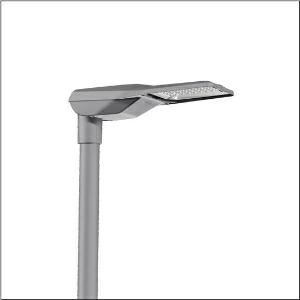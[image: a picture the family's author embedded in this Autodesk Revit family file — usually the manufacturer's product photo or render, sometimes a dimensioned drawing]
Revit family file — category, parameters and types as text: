
# Revit family: streetlight_sl_21_iq_mini___st0_5a_5xe2b41g08jb_20f7
name_source: partatom
category: Lighting Fixtures
units: mm (PartAtom-declared; Revit-internal decimal feet)

## family parameters
Cut with Voids When Loaded = No
Host = Face
Light Source = No
Part Type = Normal
Room Calculation Point = No
Round Connector Dimension = Use Diameter
Shared = No

## types (1)
- --- (1 x LED, 11290 lm, 71.6 W, 4000K)
    Apparent Load = 72 VA
    CIE Flux Codes = 43 76 97 100 100
    Color Rendering = 70
    Color Temperature = 4000K
    Default Elevation = 1800 mm
    Description = Streetlight SL 21 iQ mini, mast luminaire, primary light control with lens, of PMMA, primary optical cover: cover, of toughened safety glass, transparent, light distribution: ST0.5a, light emission: direct distribution, primary light characteristic: asymmetric, installation type: post-top, side-entry, LED, High Power LED, rated luminous flux: 11.290lm, luminous efficacy: 158lm/W, light colour: 740, colour temperature: 4000K, control: Street-Remote, Auto-Match, Temp-Guard, Lumen-Switch, Night-Set, Smart-Wire, Light-Fading, Desk-Remote (wireless, voltage-free reading and setting of iQ features in the workshop via application-optimized NFC function/RFID function), optimised constant luminous flux control (CLO 2.0), presetting dimming linear, mains connection: 220..240V, AC, 50/60Hz, start of lifetime: 72W, end of service life: 75W, reduction: 33W, luminaire housing, of diecast aluminium, powder-coated, Siteco® metallic grey (DB 702S), corrosivity category C5 mid according to DIN EN ISO 12944, please order mast flange separately, inclination adjustable: 0°, 5°, 10°, 15°, sealing non-destructively replaceable, multi-level sealing system, length: 628mm, width: 235mm, height: 110mm, mast flange for spigot size: 42mm (side-entry): 5XC10008XM4, 60/48mm (side-entry/post-top): 5XC10108XM2, 76/60mm (side-entry/post-top): 5XC10108XM1, protection rating (complete): IP66, insulation class (complete): insulation class II (safety insulation), certification: CE, ENEC, ENEC+, VDE, impact resistance: IK09, permissible operating ambient temperature for outdoor applications: -40..+50°C, standard-compliant lighting for roads and squares, packaging unit: 1 piece

Light Distribution: ST0.5a
    Height = 110 mm
    Lamp = 1 x LED
    Lamp Light Flux = 11290 lm
    Lamp Power = 71.6 W
    Lamp count = 1
    Length = 625 mm
    Luminous efficacy = 158 lm/W
    Manufacturer = Siteco
    ModVariant = No
    Model = 5XE2B41G08JB
    Number of Poles = 1
    OnlyDefault = Yes
    Power Factor = 1
    Product Name = Streetlight SL 21 iQ mini | ST0.5a
    Product group = mast luminaire | pylon top
    ProductGroupID = 6100
    Protection Class = Protection class II
    Protection Degree = IP 66
    RLX_Detail_Level = 1
    RLX_Emergency_Light_Flux = 0 lm
    RLX_Emergency_Type = 0
    RLX_Emergency_Type_DB = No
    RlxData = <blob elided: 103425 chars, md5=60cc6fd3>
    Socket = socket
    Standby Power = 0 W
    System Light Flux = 11290 lm
    System Power = 72 W
    Type Comments = factory setting: luminous flux: 100 % | dim-lin: 254 | 746 mA
    Type Image = l_1003519.jpg
    URL = http://relux.com
    VarID = @adj_104777
    Voltage = 0 V
    Weight = 0.00 kg
    Width = 234 mm

## geometry (parser evidence)
native form markers: Blend x4, Sweep x11
no freeform markers — native parametric forms only
